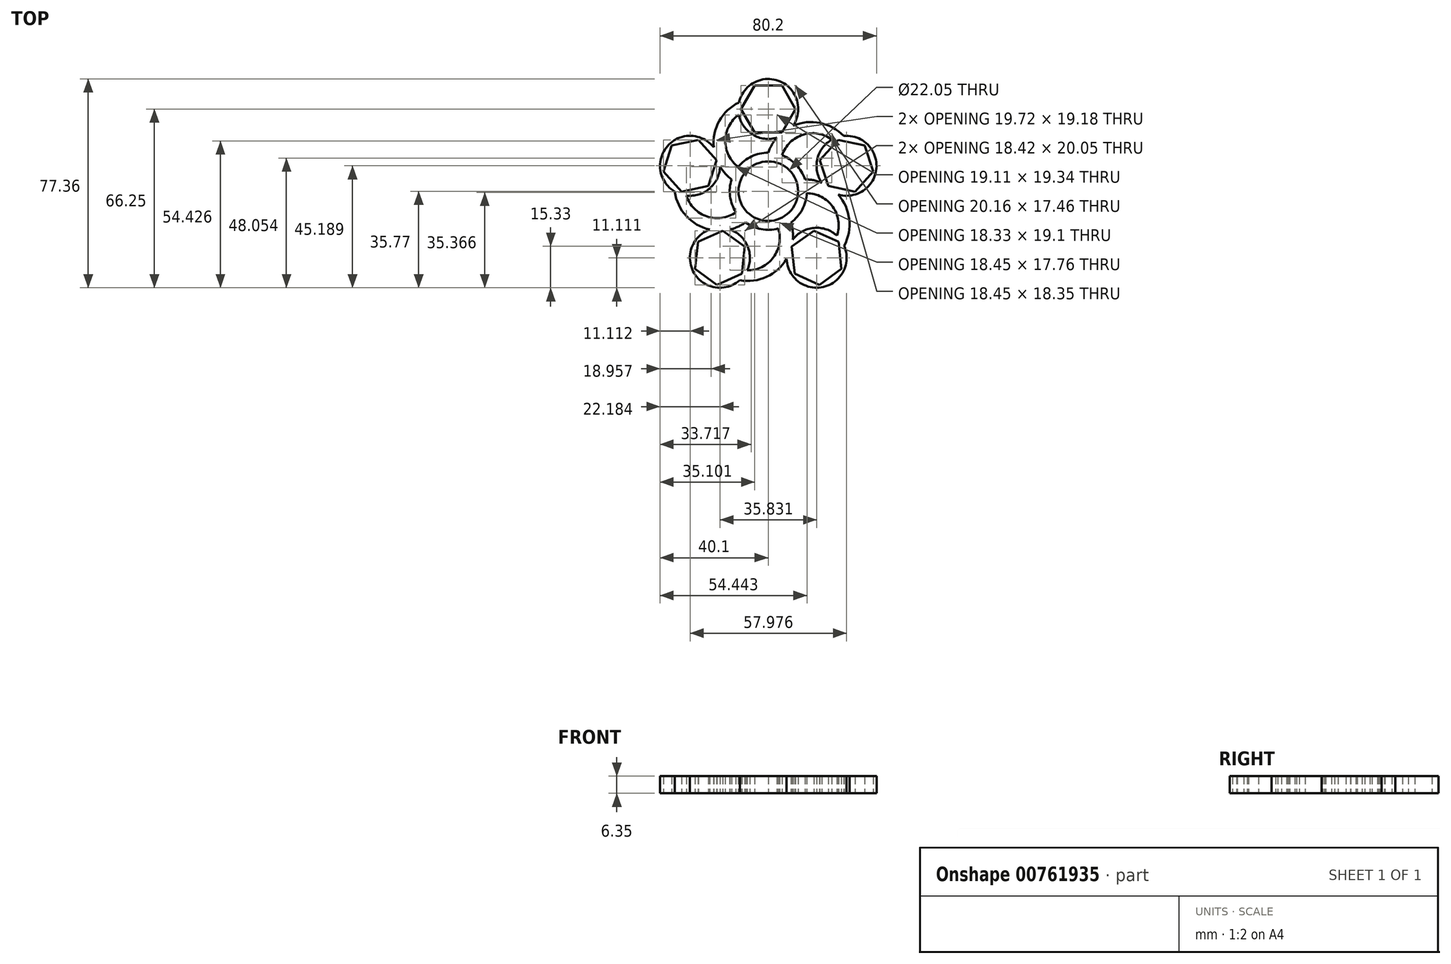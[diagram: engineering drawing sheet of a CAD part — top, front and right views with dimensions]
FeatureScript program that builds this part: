
annotation { "Feature Type Name" : "Feature", "Feature Type Description" : "" }
export const myFeature = defineFeature(function(context is Context, id is Id, definition is map)
    precondition{}
    {
        {
            var Q0;
            Q0=qCreatedBy(makeId("Top.planeOp"),FACE);
            var sketch = newSketch(context, id + "F0", { "sketchPlane" : qUnion([Q0])});
            skCircle(sketch, "E0", {"center": v(0, 0) * mm, "radius": 14.29 * mm});
            skCircle(sketch, "E1", {"center": v(0, 0) * mm, "radius": 11.02 * mm});
            skCircle(sketch, "E2", {"center": v(0, 30.48) * mm, "radius": 11.11 * mm});
            skCircle(sketch, "E3.cCircle", {"center": v(0, 30.48) * mm, "radius": 8.73 * mm, "construction": true});
            skLineSegment(sketch, "E3.0", {"start": v(5.04, 21.75) * mm, "end": v(-5.04, 21.75) * mm});
            skLineSegment(sketch, "E3.1", {"start": v(-5.04, 21.75) * mm, "end": v(-10.08, 30.48) * mm});
            skLineSegment(sketch, "E3.2", {"start": v(-10.08, 30.48) * mm, "end": v(-5.04, 39.21) * mm});
            skLineSegment(sketch, "E3.3", {"start": v(-5.04, 39.21) * mm, "end": v(5.04, 39.21) * mm});
            skLineSegment(sketch, "E3.4", {"start": v(5.04, 39.21) * mm, "end": v(10.08, 30.48) * mm});
            skLineSegment(sketch, "E3.5", {"start": v(10.08, 30.48) * mm, "end": v(5.04, 21.75) * mm});
            skPoint(sketch, "E3.0.midPoint", {"position": v(0, 21.75) * mm});
            skArc(sketch, "E4", {"start": v(-10.9, 28.32) * mm, "mid": v(-15.94, 18.7) * mm, "end": v(-11.1, 8.99) * mm});
            skArc(sketch, "E5", {"start": v(-10.85, 32.9) * mm, "mid": v(-20.23, 19.43) * mm, "end": v(-13.59, 4.42) * mm});
            skLineSegment(sketch, "E6.1.0", {"start": v(-32.1, -0.17) * mm, "end": v(-38.85, 7.32) * mm});
            skCircle(sketch, "E6.1.1", {"center": v(-28.99, 9.42) * mm, "radius": 8.73 * mm, "construction": true});
            skCircle(sketch, "E6.1.2", {"center": v(-28.99, 9.42) * mm, "radius": 11.11 * mm});
            skPoint(sketch, "E6.1.3", {"position": v(-20.68, 6.72) * mm});
            skLineSegment(sketch, "E6.1.4", {"start": v(-35.73, 16.91) * mm, "end": v(-25.87, 19) * mm});
            skLineSegment(sketch, "E6.1.5", {"start": v(-38.85, 7.32) * mm, "end": v(-35.73, 16.91) * mm});
            skLineSegment(sketch, "E6.1.6", {"start": v(-22.24, 1.93) * mm, "end": v(-32.1, -0.17) * mm});
            skLineSegment(sketch, "E6.1.7", {"start": v(-19.13, 11.51) * mm, "end": v(-22.24, 1.93) * mm});
            skLineSegment(sketch, "E6.1.8", {"start": v(-25.87, 19) * mm, "end": v(-19.13, 11.51) * mm});
            skArc(sketch, "E6.1.9", {"start": v(-34.64, -0.15) * mm, "mid": v(-24.73, -13.23) * mm, "end": v(-8.4, -11.56) * mm});
            skLineSegment(sketch, "E6.2.0", {"start": v(-9.76, -30.58) * mm, "end": v(-18.97, -34.69) * mm});
            skCircle(sketch, "E6.2.1", {"center": v(-17.92, -24.66) * mm, "radius": 8.73 * mm, "construction": true});
            skCircle(sketch, "E6.2.2", {"center": v(-17.92, -24.66) * mm, "radius": 11.11 * mm});
            skPoint(sketch, "E6.2.3", {"position": v(-12.78, -17.6) * mm});
            skLineSegment(sketch, "E6.2.4", {"start": v(-27.13, -28.76) * mm, "end": v(-26.07, -18.73) * mm});
            skLineSegment(sketch, "E6.2.5", {"start": v(-18.97, -34.69) * mm, "end": v(-27.13, -28.76) * mm});
            skLineSegment(sketch, "E6.2.6", {"start": v(-8.7, -20.56) * mm, "end": v(-9.76, -30.58) * mm});
            skLineSegment(sketch, "E6.2.7", {"start": v(-16.86, -14.63) * mm, "end": v(-8.7, -20.56) * mm});
            skLineSegment(sketch, "E6.2.8", {"start": v(-26.07, -18.73) * mm, "end": v(-16.86, -14.63) * mm});
            skArc(sketch, "E6.2.9", {"start": v(-10.56, -32.99) * mm, "mid": v(4.94, -27.6) * mm, "end": v(8.4, -11.56) * mm});
            skLineSegment(sketch, "E6.3.0", {"start": v(26.07, -18.73) * mm, "end": v(27.13, -28.76) * mm});
            skCircle(sketch, "E6.3.1", {"center": v(17.92, -24.66) * mm, "radius": 8.73 * mm, "construction": true});
            skCircle(sketch, "E6.3.2", {"center": v(17.92, -24.66) * mm, "radius": 11.11 * mm});
            skPoint(sketch, "E6.3.3", {"position": v(12.78, -17.6) * mm});
            skLineSegment(sketch, "E6.3.4", {"start": v(18.97, -34.69) * mm, "end": v(9.76, -30.58) * mm});
            skLineSegment(sketch, "E6.3.5", {"start": v(27.13, -28.76) * mm, "end": v(18.97, -34.69) * mm});
            skLineSegment(sketch, "E6.3.6", {"start": v(16.86, -14.63) * mm, "end": v(26.07, -18.73) * mm});
            skLineSegment(sketch, "E6.3.7", {"start": v(8.7, -20.56) * mm, "end": v(16.86, -14.63) * mm});
            skLineSegment(sketch, "E6.3.8", {"start": v(9.76, -30.58) * mm, "end": v(8.7, -20.56) * mm});
            skArc(sketch, "E6.3.9", {"start": v(28.11, -20.24) * mm, "mid": v(27.78, -3.83) * mm, "end": v(13.59, 4.41) * mm});
            skLineSegment(sketch, "E6.4.0", {"start": v(25.87, 19) * mm, "end": v(35.73, 16.91) * mm});
            skCircle(sketch, "E6.4.1", {"center": v(28.99, 9.42) * mm, "radius": 8.73 * mm, "construction": true});
            skCircle(sketch, "E6.4.2", {"center": v(28.99, 9.42) * mm, "radius": 11.11 * mm});
            skPoint(sketch, "E6.4.3", {"position": v(20.68, 6.72) * mm});
            skLineSegment(sketch, "E6.4.4", {"start": v(38.85, 7.32) * mm, "end": v(32.1, -0.17) * mm});
            skLineSegment(sketch, "E6.4.5", {"start": v(35.73, 16.91) * mm, "end": v(38.85, 7.32) * mm});
            skLineSegment(sketch, "E6.4.6", {"start": v(19.13, 11.51) * mm, "end": v(25.87, 19) * mm});
            skLineSegment(sketch, "E6.4.7", {"start": v(22.24, 1.93) * mm, "end": v(19.13, 11.51) * mm});
            skLineSegment(sketch, "E6.4.8", {"start": v(32.1, -0.17) * mm, "end": v(22.24, 1.93) * mm});
            skArc(sketch, "E6.4.9", {"start": v(27.93, 20.48) * mm, "mid": v(12.23, 25.24) * mm, "end": v(0, 14.29) * mm});
            skArc(sketch, "E7.1.0", {"start": v(-30.3, -1.62) * mm, "mid": v(-22.72, -9.38) * mm, "end": v(-11.98, -7.79) * mm});
            skArc(sketch, "E7.2.0", {"start": v(-7.83, -29.32) * mm, "mid": v(1.9, -24.5) * mm, "end": v(3.7, -13.8) * mm});
            skArc(sketch, "E7.3.0", {"start": v(25.47, -16.5) * mm, "mid": v(23.9, -5.77) * mm, "end": v(14.27, -0.74) * mm});
            skArc(sketch, "E7.4.0", {"start": v(23.57, 19.12) * mm, "mid": v(12.87, 20.94) * mm, "end": v(5.12, 13.34) * mm});
            skSolve(sketch);
        }
        {
            var Q0;
            Q0=makeQuery(id+"F0.imprint","IMPRINT",FACE,{"disambiguationData":[TD([[makeQuery(id+"F0.imprint","IMPRINT",EDGE,{"derivedFrom":sQuery(id+"F0.wireOp",EDGE,"E3.0")}),1.0]])]});
            var Q1;
            Q1=makeQuery(id+"F0.imprint","IMPRINT",FACE,{"disambiguationData":[TD([[makeQuery(id+"F0.imprint","IMPRINT",EDGE,{"derivedFrom":sQuery(id+"F0.wireOp",EDGE,"E6.1.0")}),1.0]])]});
            var Q2;
            {var subQ7=sQuery(id+"F0.wireOp",EDGE,"E7.1.0");Q2=makeQuery(id+"F0.imprint","IMPRINT",FACE,{"disambiguationData":[TD([[makeQuery(id+"F0.imprint","IMPRINT",EDGE,{"derivedFrom":subQ7}),-1.0]])]});}
            var Q3;
            {var subQ5=sQuery(id+"F0.wireOp",EDGE,"E4");Q3=makeQuery(id+"F0.imprint","IMPRINT",FACE,{"disambiguationData":[TD([[makeQuery(id+"F0.imprint","IMPRINT",EDGE,{"derivedFrom":subQ5}),-1.0]])]});}
            var Q4;
            {var subQ0=sQuery(id+"F0.wireOp",EDGE,"E6.1.2");var subQ1=sQuery(id+"F0.wireOp",EDGE,"E5");var subQ2=makeQuery(id+"F0.imprint","INTERSECT",VERTEX,{"disambiguationData":[OD(0.0)],"derivedFrom":[subQ1,subQ0]});Q4=makeQuery(id+"F0.imprint","IMPRINT",FACE,{"disambiguationData":[TD([[makeQuery(id+"F0.imprint","IMPRINT",EDGE,{"disambiguationData":[TD([[subQ2,-1.0]])],"derivedFrom":subQ1}),1.0]])]});}
            var Q5;
            {var subQ5=sQuery(id+"F0.wireOp",EDGE,"E7.4.0");Q5=makeQuery(id+"F0.imprint","IMPRINT",FACE,{"disambiguationData":[TD([[makeQuery(id+"F0.imprint","IMPRINT",EDGE,{"derivedFrom":subQ5}),-1.0]])]});}
            var Q6;
            {var subQ0=sQuery(id+"F0.wireOp",EDGE,"E6.4.2");var subQ1=sQuery(id+"F0.wireOp",EDGE,"E6.3.9");var subQ2=makeQuery(id+"F0.imprint","INTERSECT",VERTEX,{"disambiguationData":[OD(0.0)],"derivedFrom":[subQ1,subQ0]});Q6=makeQuery(id+"F0.imprint","IMPRINT",FACE,{"disambiguationData":[TD([[makeQuery(id+"F0.imprint","IMPRINT",EDGE,{"disambiguationData":[TD([[subQ2,-1.0]])],"derivedFrom":subQ1}),1.0]])]});}
            var Q7;
            {var subQ7=sQuery(id+"F0.wireOp",EDGE,"E7.3.0");Q7=makeQuery(id+"F0.imprint","IMPRINT",FACE,{"disambiguationData":[TD([[makeQuery(id+"F0.imprint","IMPRINT",EDGE,{"derivedFrom":subQ7}),-1.0]])]});}
            var Q8;
            Q8=makeQuery(id+"F0.imprint","IMPRINT",FACE,{"disambiguationData":[TD([[makeQuery(id+"F0.imprint","IMPRINT",EDGE,{"derivedFrom":sQuery(id+"F0.wireOp",EDGE,"E6.4.0")}),1.0]])]});
            var Q9;
            {var subQ7=sQuery(id+"F0.wireOp",EDGE,"E7.2.0");Q9=makeQuery(id+"F0.imprint","IMPRINT",FACE,{"disambiguationData":[TD([[makeQuery(id+"F0.imprint","IMPRINT",EDGE,{"derivedFrom":subQ7}),-1.0]])]});}
            var Q10;
            {var subQ0=sQuery(id+"F0.wireOp",EDGE,"E6.2.2");var subQ1=sQuery(id+"F0.wireOp",EDGE,"E6.1.9");var subQ2=makeQuery(id+"F0.imprint","INTERSECT",VERTEX,{"disambiguationData":[OD(0.0)],"derivedFrom":[subQ1,subQ0]});Q10=makeQuery(id+"F0.imprint","IMPRINT",FACE,{"disambiguationData":[TD([[makeQuery(id+"F0.imprint","IMPRINT",EDGE,{"disambiguationData":[TD([[subQ2,-1.0]])],"derivedFrom":subQ1}),1.0]])]});}
            var Q11;
            Q11=makeQuery(id+"F0.imprint","IMPRINT",FACE,{"disambiguationData":[TD([[makeQuery(id+"F0.imprint","IMPRINT",EDGE,{"derivedFrom":sQuery(id+"F0.wireOp",EDGE,"E6.2.0")}),1.0]])]});
            var Q12;
            {var subQ0=sQuery(id+"F0.wireOp",EDGE,"E6.3.2");var subQ1=sQuery(id+"F0.wireOp",EDGE,"E6.2.9");var subQ2=makeQuery(id+"F0.imprint","INTERSECT",VERTEX,{"disambiguationData":[OD(0.0)],"derivedFrom":[subQ1,subQ0]});Q12=makeQuery(id+"F0.imprint","IMPRINT",FACE,{"disambiguationData":[TD([[makeQuery(id+"F0.imprint","IMPRINT",EDGE,{"disambiguationData":[TD([[subQ2,-1.0]])],"derivedFrom":subQ1}),1.0]])]});}
            var Q13;
            Q13=makeQuery(id+"F0.imprint","IMPRINT",FACE,{"disambiguationData":[TD([[makeQuery(id+"F0.imprint","IMPRINT",EDGE,{"derivedFrom":sQuery(id+"F0.wireOp",EDGE,"E6.3.0")}),1.0]])]});
            var Q14;
            Q14=makeQuery(id+"F0.imprint","IMPRINT",FACE,{"disambiguationData":[TD([[makeQuery(id+"F0.imprint","IMPRINT",EDGE,{"derivedFrom":sQuery(id+"F0.wireOp",EDGE,"E1")}),-1.0]])]});
            var Q15;
            {var subQ0=sQuery(id+"F0.wireOp",EDGE,"E6.4.9");var subQ1=sQuery(id+"F0.wireOp",EDGE,"E2");var subQ2=makeQuery(id+"F0.imprint","INTERSECT",VERTEX,{"disambiguationData":[OD(0.0)],"derivedFrom":[subQ1,subQ0]});Q15=makeQuery(id+"F0.imprint","IMPRINT",FACE,{"disambiguationData":[TD([[makeQuery(id+"F0.imprint","IMPRINT",EDGE,{"disambiguationData":[TD([[subQ2,1.0]])],"derivedFrom":subQ1}),1.0]])]});}
            extrude(context, id + "F1", {"entities" : qUnion([Q0, Q1, Q2, Q3, Q4, Q5, Q6, Q7, Q8, Q9, Q10, Q11, Q12, Q13, Q14, Q15]), "depth" : 6.35 * mm, "offsetDistance" : 25.4 * mm});
        }
    });
